# Revit family: CORH04-R-DL-BK-WH
name_source: partatom
category: Lighting Fixtures
units: mm (PartAtom-declared; Revit-internal decimal feet)

## family parameters
Cut with Voids When Loaded = Yes
Host = Face
Light Source = Yes
Maintain Annotation Orientation = No
Part Type = Normal
Room Calculation Point = No
Round Connector Dimension = Use Diameter
Shared = No

## types (8) — shared parameters
CRI = 90
Color Filter = 16777215
Default Elevation = 0' - 0"
Dimming Lamp Color Temperature Shift = <None>
Lamp = LED
Load Classification = Lighting
Manufacturer = Above All Lighting
Model = CORH04-R-DL-BK-WH
Power Factor = 0.9
Tilt Angle = 90.00°
URL = https://www.abovealllighting.com

## per-type parameters (varying)
| type | Beam Angle | Photometric Web File | Wattage Comments |
| CORH04-R-DL-BK-WH-20W-3000K-15D | 15.00° | CORH04-R-DL-20W-3000K-CRI90-15D.IES | 20W |
| CORH04-R-DL-BK-WH-20W-3000K-24D | 24.00° | CORH04-R-DL-20W-3000K-CRI90-24D.IES | 20W |
| CORH04-R-DL-BK-WH-20W-3000K-55D | 55.00° | CORH04-R-DL-20W-3000K-CRI90-55D.IES | 20W |
| CORH04-R-DL-BK-WH-25W-3000K-15D | 15.00° | CORH04-R-DL-25W-3000K-CRI90-15D.IES | 25W |
| CORH04-R-DL-BK-WH-25W-3000K-24D | 24.00° | CORH04-R-DL-25W-3000K-CRI90-24D.IES | 25W |
| CORH04-R-DL-BK-WH-25W-3000K-38D | 38.00° | CORH04-R-DL-25W-3000K-CRI90-38D.IES | 25W |
| CORH04-R-DL-BK-WH-25W-3000K-55D | 55.00° | CORH04-R-DL-25W-3000K-CRI90-55D.IES | 25W |
| CORH04-R-DL-BK-WH-20W-3000K-38D | 38.00° | CORH04-R-DL-20W-3000K-CRI90-38D.IES | 20W |

## geometry (parser evidence)
native form markers: Sweep x5
no freeform markers — native parametric forms only
